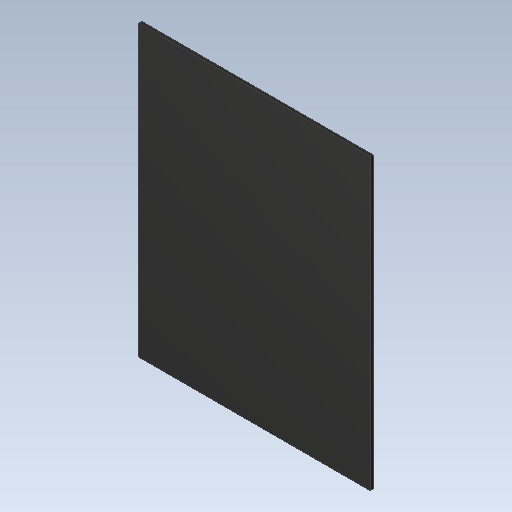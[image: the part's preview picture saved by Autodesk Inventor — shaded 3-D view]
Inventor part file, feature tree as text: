
AUTODESK INVENTOR PART (.ipt)
format: ipt  version: 2023 (Build 270158000, 158)  size: 90,624 bytes
history: imported  units: in
note: dims shown in document units (in); Inventor stores cm internally (conversion verified against a paired STEP export)
features: imported_body x1
ambient origin geometry x8: Origin, YZ Plane, XZ Plane, XY Plane, X Axis, Y Axis, Z Axis, Center Point
bodies: Solid1 (imported_parasolid), Body1 (imported_parasolid)
feature tree (1):
  imported_body  NMx_Import_Brep_tag  [imported B-rep: ~6 faces, bbox_mm=[8.191, 10.25, 0.1]]
